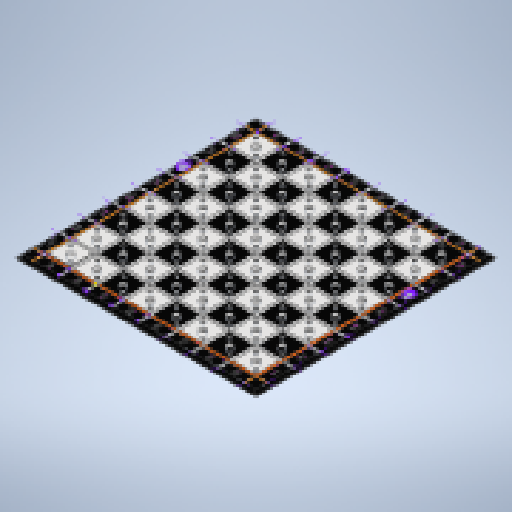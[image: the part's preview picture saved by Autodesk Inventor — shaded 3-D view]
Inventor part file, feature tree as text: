
AUTODESK INVENTOR PART (.ipt)
format: ipt  version: 2024.1 (Build 281209000, 209)  size: 1,927,168 bytes
history: native  units: in
note: dims shown in document units (in); Inventor stores cm internally (conversion verified against a paired STEP export)
features: projected_geometry x14, extrude x11, sketch x11, other x5, chamfer x5, pattern_linear x1
ambient origin geometry x8: Origin, YZ Plane, XZ Plane, XY Plane, X Axis, Y Axis, Z Axis, Center Point
bodies: Body1 (feature_tree), Body2 (feature_tree)
feature tree (47):
  other  "top-plate"
  extrude  "Extrusion1"  Depth=1.0039in
  chamfer  "Chamfer1"  Distance=0.1102in
  extrude  "Extrusion2"  Depth=0.0591in
  pattern_linear  "Rectangular Pattern1"  Count1=8 Spacing1=1.0039in
  extrude  "Extrusion5"  Depth=0.5118in
  extrude  "Extrusion6"  Depth=0.0433in TaperAngle=45.0deg
  extrude  "Extrusion4"  Depth=0.0236in TaperAngle=0.0deg
  chamfer  "Chamfer3"  Distance=0.0394in
  chamfer  "Chamfer4"  [1 undecoded]
  extrude  "Extrusion8"  Depth=0.0118in TaperAngle=0.0deg
  extrude  "Extrusion9"  Depth=0.0157in
  extrude  "Extrusion10"  Depth=0.0157in
  extrude  "Extrusion11"  Depth=0.0157in
  extrude  "Extrusion12"  Depth=0.0157in
  chamfer  "Chamfer5"  Distance=0.1575in
  extrude  "Extrusion13"  Depth=0.0157in
  chamfer  "Chamfer6"  Distance=0.1575in
  other  "Work Point1"
  other  "Work Point2"
  other  "Work Point3"
  sketch  "Sketch1"  dims[d0=1.0039in d1=1.0039in d2=0.1102in d3=0.0in]
  sketch  "Sketch2"  dims[d4=0.0591in d5=0.0787in d6=45.0deg d7=0.2362in]
  sketch  "Sketch4"  dims[d8=1.0039in]
  projected_geometry  "Projected Loop1"
  sketch  "Sketch5"  dims[d9=0.502in]
  projected_geometry  "Projected Loop2"
  projected_geometry  "Projected Loop3"
  sketch  "Sketch6"  dims[d10=1.0039in]
  projected_geometry  "Projected Loop4"
  sketch  "Sketch8"  dims[d11=0.502in]
  sketch  "Sketch9"  dims[d12=0.0984in d13=0.0in d23=3.1496in d25=1.0039in]
  projected_geometry  "Projected Loop5"
  projected_geometry  "Projected Loop6"
  projected_geometry  "Projected Loop7"
  projected_geometry  "Projected Loop8"
  projected_geometry  "Projected Loop9"
  projected_geometry  "Projected Loop10"
  projected_geometry  "Projected Loop11"
  projected_geometry  "Projected Loop12"
  projected_geometry  "Projected Loop13"
  sketch  "Sketch10"  dims[d26=3.1496in d28=1.0039in d29=0.5118in]
  sketch  "Sketch11"  dims[d30=0.1575in d31=0.0in d32=0.0433in d33=0.0787in d34=45.0deg]
  sketch  "Sketch12"  dims[d35=0.0984in d36=0.0787in d37=45.0deg d38=0.0236in d39=0.0in d40=0.0394in d41=0.0in d53=0.0in d54=0.0in]
  projected_geometry  "Projected Loop14"
  other  "top-caps"
  sketch  "Sketch13"  dims[d55=0.0in d56=0.0in d57=0.0118in d58=0.0in d59=0.1378in d60=0.1575in d61=0.1575in d62=0.1575in d63=0.1575in d64=3.1496in d66=1.0039in d67=3.1496in d69=1.0039in d72=0.1575in d73=0.1575in d74=0.0591in d75=0.0in d76=0.0157in d77=0.0in d78=0.0157in d79=0.0787in d80=45.0deg d81=0.0079in d82=0.0079in d83=0.0472in d84=0.0in d85=0.0157in d86=0.0787in d87=45.0deg]
note: 1 required parameter value undecoded (feature->parameter linkage not recoverable at this tier; creation-order binding heuristic only, values carry confidence <= 0.55)
